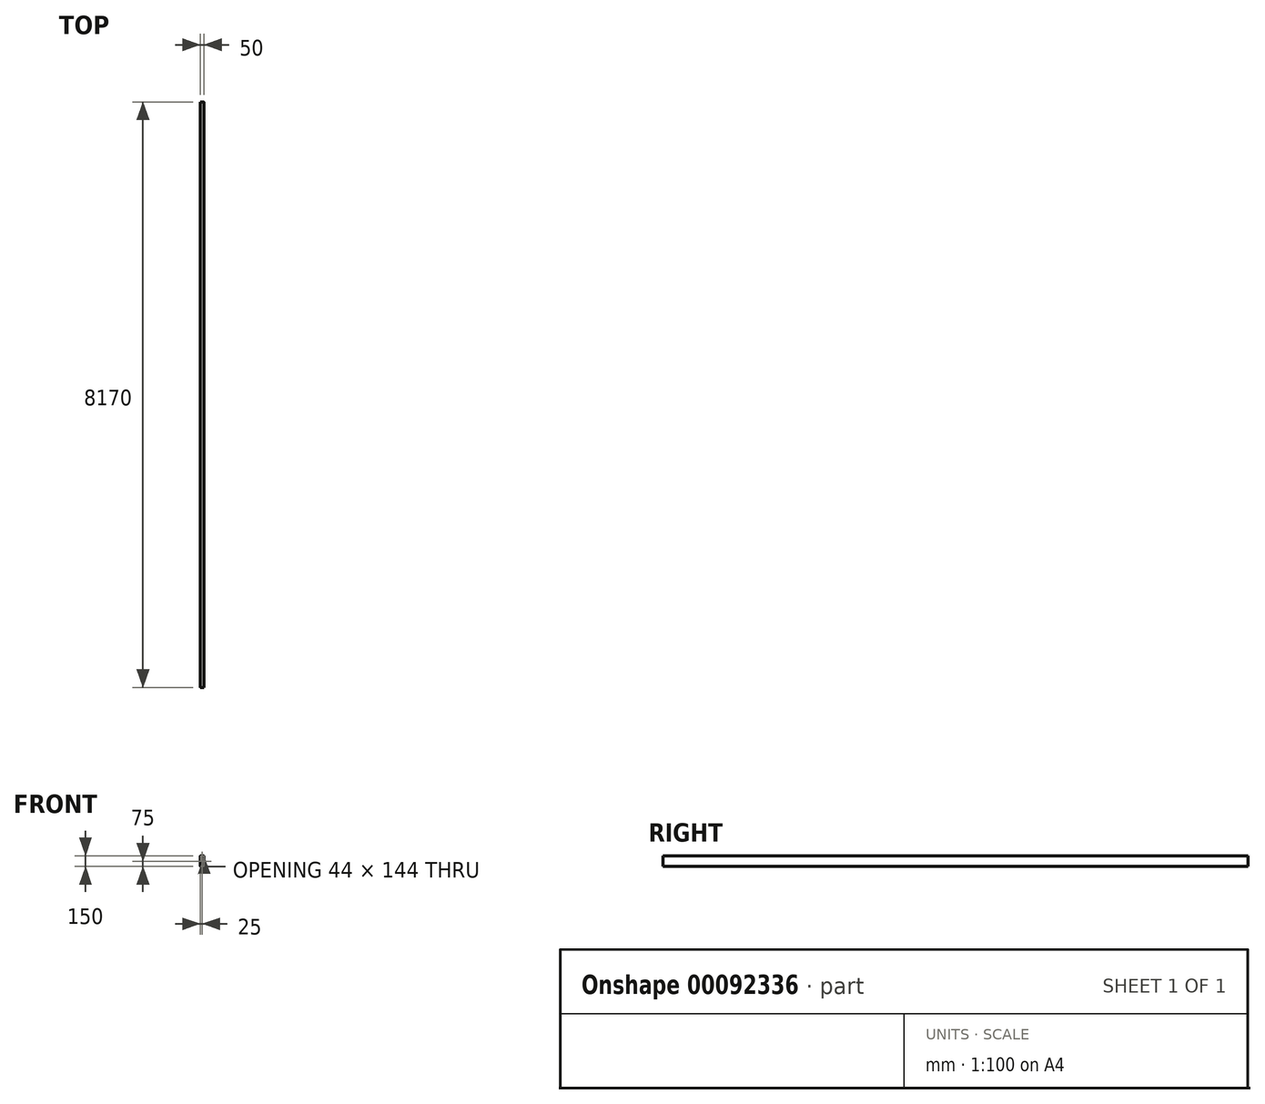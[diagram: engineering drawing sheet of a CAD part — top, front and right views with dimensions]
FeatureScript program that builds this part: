
annotation { "Feature Type Name" : "Feature", "Feature Type Description" : "" }
export const myFeature = defineFeature(function(context is Context, id is Id, definition is map)
    precondition{}
    {
        {
            var Q0;
            Q0=qCreatedBy(makeId("Front.planeOp"),FACE);
            var sketch = newSketch(context, id + "F0", { "sketchPlane" : qUnion([Q0])});
            skLineSegment(sketch, "E0.bottom", {"start": v(2.4, 0) * mm, "end": v(47.6, 0) * mm});
            skLineSegment(sketch, "E0.top", {"start": v(2.4, 150) * mm, "end": v(47.6, 150) * mm});
            skLineSegment(sketch, "E0.left", {"start": v(0, 2.4) * mm, "end": v(0, 147.6) * mm});
            skLineSegment(sketch, "E0.right", {"start": v(50, 2.4) * mm, "end": v(50, 147.6) * mm});
            skPoint(sketch, "E1.visualSharp", {"position": v(0, 150) * mm});
            skArc(sketch, "E1.filletArc", {"start": v(2.4, 150) * mm, "mid": v(0.7, 149.3) * mm, "end": v(0, 147.6) * mm});
            skPoint(sketch, "E2.visualSharp", {"position": v(50, 150) * mm});
            skArc(sketch, "E2.filletArc", {"start": v(50, 147.6) * mm, "mid": v(49.3, 149.3) * mm, "end": v(47.6, 150) * mm});
            skPoint(sketch, "E3.visualSharp", {"position": v(0, 0) * mm});
            skArc(sketch, "E3.filletArc", {"start": v(0, 2.4) * mm, "mid": v(0.7, 0.7) * mm, "end": v(2.4, 0) * mm});
            skPoint(sketch, "E4.visualSharp", {"position": v(50, 0) * mm});
            skArc(sketch, "E4.filletArc", {"start": v(47.6, 0) * mm, "mid": v(49.3, 0.7) * mm, "end": v(50, 2.4) * mm});
            skLineSegment(sketch, "E5.0", {"start": v(3, 5.4) * mm, "end": v(3, 144.6) * mm});
            skLineSegment(sketch, "E6.0", {"start": v(5.4, 147) * mm, "end": v(44.6, 147) * mm});
            skLineSegment(sketch, "E7.0", {"start": v(47, 5.4) * mm, "end": v(47, 144.6) * mm});
            skLineSegment(sketch, "E8.0", {"start": v(5.4, 3) * mm, "end": v(44.6, 3) * mm});
            skArc(sketch, "E9.filletArc", {"start": v(5.4, 147) * mm, "mid": v(3.7, 146.3) * mm, "end": v(3, 144.6) * mm});
            skArc(sketch, "E10.filletArc", {"start": v(3, 5.4) * mm, "mid": v(3.7, 3.7) * mm, "end": v(5.4, 3) * mm});
            skArc(sketch, "E11.filletArc", {"start": v(47, 144.6) * mm, "mid": v(46.3, 146.3) * mm, "end": v(44.6, 147) * mm});
            skArc(sketch, "E12.filletArc", {"start": v(44.6, 3) * mm, "mid": v(46.3, 3.7) * mm, "end": v(47, 5.4) * mm});
            skSolve(sketch);
        }
        {
            var Q0;
            Q0=qSketchRegion(id+"F0",true);
            extrude(context, id + "F1", {"entities" : qUnion([Q0]), "depth" : 8170 * mm, "offsetDistance" : 25 * mm});
        }
    });
